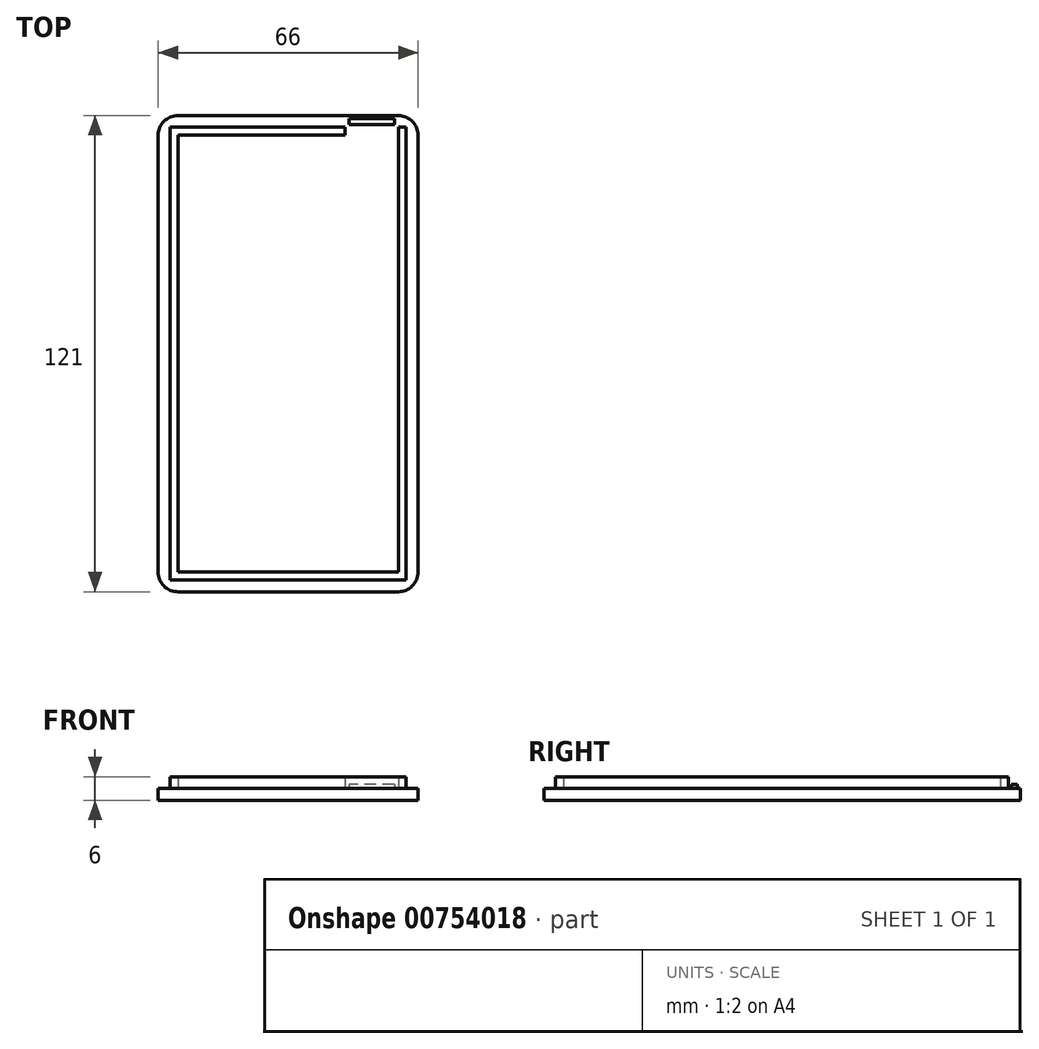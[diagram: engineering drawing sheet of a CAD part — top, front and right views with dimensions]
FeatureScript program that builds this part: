
annotation { "Feature Type Name" : "Feature", "Feature Type Description" : "" }
export const myFeature = defineFeature(function(context is Context, id is Id, definition is map)
    precondition{}
    {
        {
            var Q0;
            Q0=qCreatedBy(makeId("Top.planeOp"),FACE);
            var sketch = newSketch(context, id + "F0", { "sketchPlane" : qUnion([Q0])});
            skLineSegment(sketch, "E0", {"start": v(30, 57.5) * mm, "end": v(30, -57.5) * mm});
            skLineSegment(sketch, "E1", {"start": v(30, -57.5) * mm, "end": v(-30, -57.5) * mm});
            skLineSegment(sketch, "E2", {"start": v(-30, -57.5) * mm, "end": v(-30, 57.5) * mm});
            skLineSegment(sketch, "E3", {"start": v(-33, 60.5) * mm, "end": v(-33, -60.5) * mm});
            skLineSegment(sketch, "E4", {"start": v(-33, -60.5) * mm, "end": v(33, -60.5) * mm});
            skLineSegment(sketch, "E5", {"start": v(33, -60.5) * mm, "end": v(33, 60.5) * mm});
            skLineSegment(sketch, "E6", {"start": v(33, 60.5) * mm, "end": v(-33, 60.5) * mm});
            skLineSegment(sketch, "E7", {"start": v(28, 57.5) * mm, "end": v(28, -55.5) * mm});
            skLineSegment(sketch, "E8", {"start": v(28, -55.5) * mm, "end": v(-28, -55.5) * mm});
            skLineSegment(sketch, "E9", {"start": v(-28, -55.5) * mm, "end": v(-28, 55.5) * mm});
            skLineSegment(sketch, "E10", {"start": v(30, 57.5) * mm, "end": v(28, 57.5) * mm});
            skLineSegment(sketch, "E11", {"start": v(-30, 57.5) * mm, "end": v(14.5, 57.5) * mm});
            skLineSegment(sketch, "E12", {"start": v(14.5, 57.5) * mm, "end": v(14.5, 55.5) * mm});
            skLineSegment(sketch, "E13", {"start": v(14.5, 55.5) * mm, "end": v(-28, 55.5) * mm});
            skLineSegment(sketch, "E14", {"start": v(27, 59.75) * mm, "end": v(15.5, 59.75) * mm});
            skLineSegment(sketch, "E15", {"start": v(15.5, 59.75) * mm, "end": v(15.5, 58.25) * mm});
            skLineSegment(sketch, "E16", {"start": v(15.5, 58.25) * mm, "end": v(27, 58.25) * mm});
            skLineSegment(sketch, "E17", {"start": v(27, 58.25) * mm, "end": v(27, 59.75) * mm});
            skLineSegment(sketch, "E18", {"start": v(27, 59.75) * mm, "end": v(28, 59.75) * mm, "construction": true});
            skLineSegment(sketch, "E19", {"start": v(28, 59.75) * mm, "end": v(28, 58.25) * mm, "construction": true});
            skLineSegment(sketch, "E20", {"start": v(28, 58.25) * mm, "end": v(27, 58.25) * mm, "construction": true});
            skLineSegment(sketch, "E21", {"start": v(15.5, 59.75) * mm, "end": v(14.5, 59.75) * mm, "construction": true});
            skLineSegment(sketch, "E22", {"start": v(14.5, 59.75) * mm, "end": v(14.5, 58.25) * mm, "construction": true});
            skLineSegment(sketch, "E23", {"start": v(14.5, 58.25) * mm, "end": v(15.5, 58.25) * mm, "construction": true});
            skSolve(sketch);
        }
        {
            var Q0;
            Q0=makeQuery(id+"F0.imprint","IMPRINT",FACE,{"disambiguationData":[TD([[makeQuery(id+"F0.imprint","IMPRINT",EDGE,{"derivedFrom":sQuery(id+"F0.wireOp",EDGE,"E0")}),-1.0]])]});
            extrude(context, id + "F1", {"entities" : qUnion([Q0]), "depth" : 6 * mm, "offsetDistance" : 25 * mm});
        }
        {
            var Q0;
            Q0=makeQuery(id+"F0.imprint","IMPRINT",FACE,{"disambiguationData":[TD([[makeQuery(id+"F0.imprint","IMPRINT",EDGE,{"derivedFrom":sQuery(id+"F0.wireOp",EDGE,"E0")}),1.0]])]});
            var Q1;
            {var subQ3=sQuery(id+"F0.wireOp",EDGE,"E8");Q1=makeQuery(id+"F0.imprint","IMPRINT",FACE,{"disambiguationData":[TD([[makeQuery(id+"F0.imprint","IMPRINT",EDGE,{"derivedFrom":subQ3}),-1.0]])]});}
            extrude(context, id + "F2", {"entities" : qUnion([Q0, Q1]), "operationType" : NewBodyOperationType.ADD, "depth" : 3 * mm, "offsetDistance" : 25 * mm});
        }
        {
            var Q0;
            Q0=makeQuery(id+"F1.opExtrude","SWEPT_EDGE",EDGE,{"disambiguationData":[OSD([sQuery(id+"F0.wireOp",EDGE,"E3"),sQuery(id+"F0.wireOp",EDGE,"E6")])]});
            var Q1;
            Q1=makeQuery(id+"F1.opExtrude","SWEPT_EDGE",EDGE,{"disambiguationData":[OSD([sQuery(id+"F0.wireOp",EDGE,"E3"),sQuery(id+"F0.wireOp",EDGE,"E4")])]});
            var Q2;
            Q2=makeQuery(id+"F1.opExtrude","SWEPT_EDGE",EDGE,{"disambiguationData":[OSD([sQuery(id+"F0.wireOp",EDGE,"E4"),sQuery(id+"F0.wireOp",EDGE,"E5")])]});
            var Q3;
            Q3=makeQuery(id+"F1.opExtrude","SWEPT_EDGE",EDGE,{"disambiguationData":[OSD([sQuery(id+"F0.wireOp",EDGE,"E5"),sQuery(id+"F0.wireOp",EDGE,"E6")])]});
            var Q4;
            Q4=makeQuery(id+"F2.opExtrude","SWEPT_EDGE",EDGE,{"disambiguationData":[OSD([sQuery(id+"F0.wireOp",EDGE,"E5"),sQuery(id+"F0.wireOp",EDGE,"E6")])]});
            var Q5;
            Q5=makeQuery(id+"F2.opExtrude","SWEPT_EDGE",EDGE,{"disambiguationData":[OSD([sQuery(id+"F0.wireOp",EDGE,"E3"),sQuery(id+"F0.wireOp",EDGE,"E6")])]});
            var Q6;
            Q6=makeQuery(id+"F2.opExtrude","SWEPT_EDGE",EDGE,{"disambiguationData":[OSD([sQuery(id+"F0.wireOp",EDGE,"E4"),sQuery(id+"F0.wireOp",EDGE,"E5")])]});
            var Q7;
            Q7=makeQuery(id+"F2.opExtrude","SWEPT_EDGE",EDGE,{"disambiguationData":[OSD([sQuery(id+"F0.wireOp",EDGE,"E3"),sQuery(id+"F0.wireOp",EDGE,"E4")])]});
            fillet(context, id + "F3", {"entities" : qUnion([Q0, Q1, Q2, Q3, Q4, Q5, Q6, Q7]), "radius" : 5 * mm, "tangentPropagation" : true, "allowEdgeOverflow" : false});
        }
        {
            var Q0;
            {var subQ0=sQuery(id+"F0.wireOp",EDGE,"KUsBGPJ0-NAp7-S75a-4KwJ-NzaEf42ZQ3oD");Q0=makeQuery(id+"F0.imprint","IMPRINT",FACE,{"disambiguationData":[TD([[makeQuery(id+"F0.imprint","IMPRINT",EDGE,{"derivedFrom":subQ0}),1.0]])]});}
            var Q1;
            Q1=makeQuery(id+"F0.imprint","IMPRINT",FACE,{"disambiguationData":[TD([[makeQuery(id+"F0.imprint","IMPRINT",EDGE,{"derivedFrom":sQuery(id+"F0.wireOp",EDGE,"jFyWDwbn-r72F-b3WB-kCfz-AHK9B3nxDVlK")}),-1.0]])]});
            var Q2;
            Q2=makeQuery(id+"F0.imprint","IMPRINT",FACE,{"disambiguationData":[TD([[makeQuery(id+"F0.imprint","IMPRINT",EDGE,{"derivedFrom":sQuery(id+"F0.wireOp",EDGE,"E14")}),1.0]])]});
            extrude(context, id + "F4", {"entities" : qUnion([Q0, Q1, Q2]), "operationType" : NewBodyOperationType.ADD, "depth" : 4 * mm, "offsetDistance" : 25 * mm});
        }
    });
